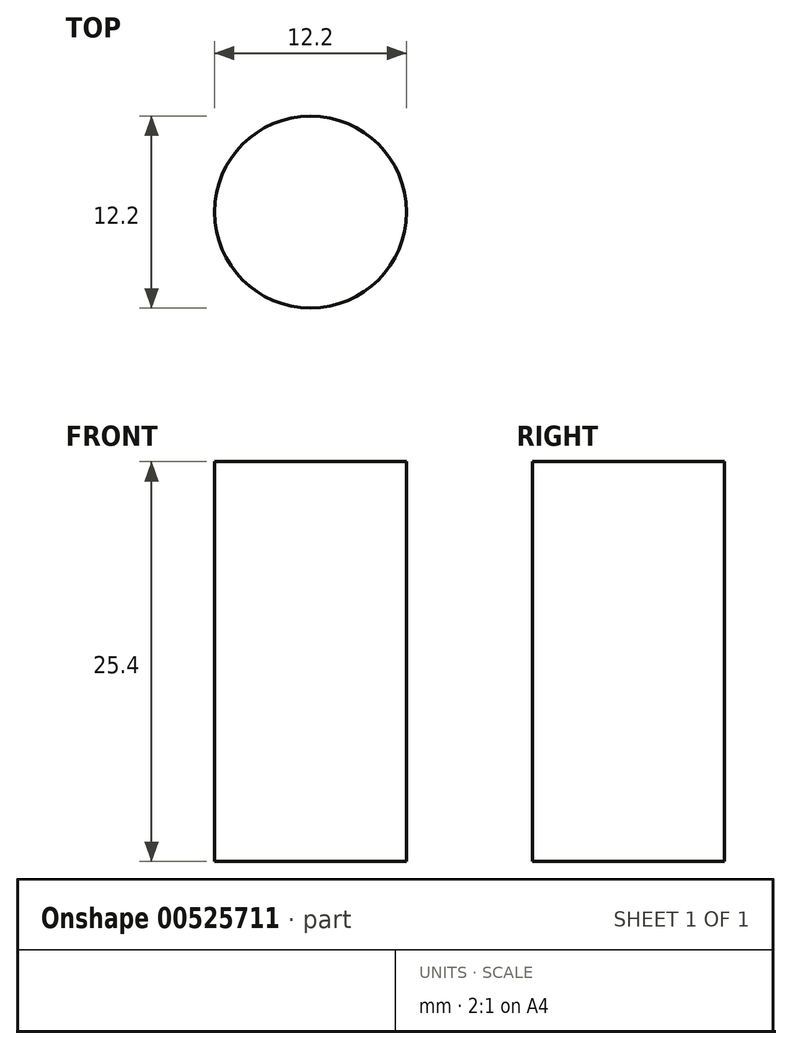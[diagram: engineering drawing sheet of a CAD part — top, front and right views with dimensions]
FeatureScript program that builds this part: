
annotation { "Feature Type Name" : "Feature", "Feature Type Description" : "" }
export const myFeature = defineFeature(function(context is Context, id is Id, definition is map)
    precondition{}
    {
        {
            var Q0;
            Q0=qCreatedBy(makeId("Top.planeOp"),FACE);
            var sketch = newSketch(context, id + "F0", { "sketchPlane" : qUnion([Q0])});
            skCircle(sketch, "E0", {"center": v(0, 0) * mm, "radius": 6.1 * mm});
            skSolve(sketch);
        }
        {
            var Q0;
            Q0 = qSketchRegion(id + "F0", true);
            extrude(context, id + "F1", {"entities" : qUnion([Q0]), "depth" : 25.4 * mm, "offsetDistance" : 25.4 * mm});
        }
    });
